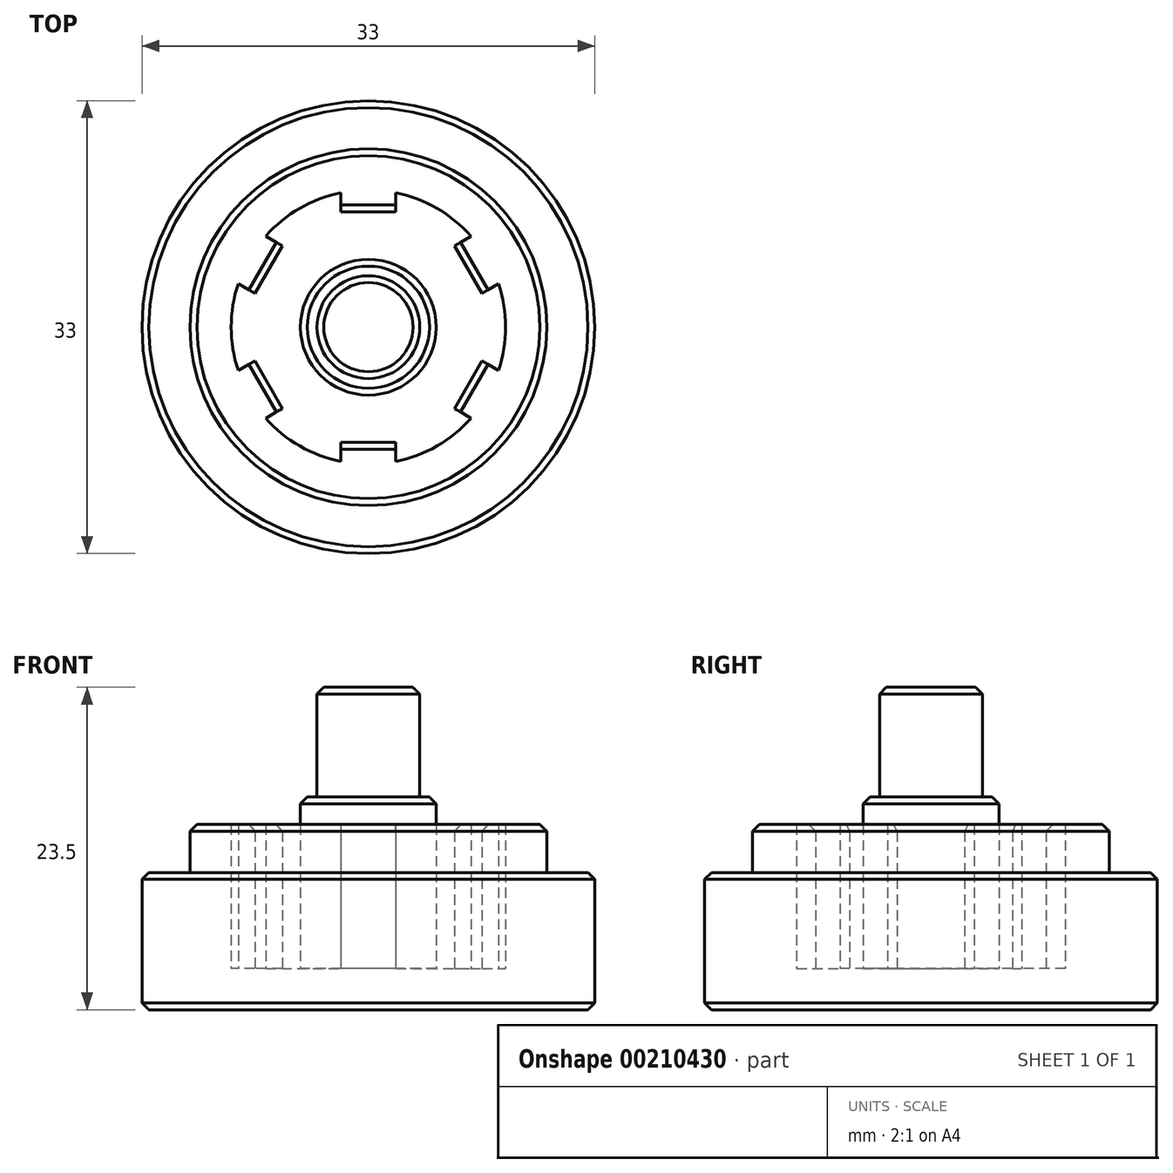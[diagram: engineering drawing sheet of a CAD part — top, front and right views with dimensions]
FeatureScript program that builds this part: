
annotation { "Feature Type Name" : "Feature", "Feature Type Description" : "" }
export const myFeature = defineFeature(function(context is Context, id is Id, definition is map)
    precondition{}
    {
        {
            var Q0;
            Q0=qCreatedBy(makeId("Top.planeOp"),FACE);
            var sketch = newSketch(context, id + "F0", { "sketchPlane" : qUnion([Q0])});
            skCircle(sketch, "E0", {"center": v(0, 0) * mm, "radius": 16.5 * mm});
            skSolve(sketch);
        }
        {
            var Q0;
            Q0 = qSketchRegion(id + "F0", true);
            extrude(context, id + "F1", {"entities" : qUnion([Q0]), "depth" : 10 * mm});
        }
        {
            var Q0;
            Q0=makeQuery(id+"F1.opExtrude","CAP_FACE",FACE,{"disambiguationData":[OSD([sQuery(id+"F0.wireOp",EDGE,"E0")])],"isStart":false});
            var sketch = newSketch(context, id + "F2", { "sketchPlane" : qUnion([Q0])});
            skArc(sketch, "E1", {"start": v(-2, 9.8) * mm, "mid": v(-5, 8.66) * mm, "end": v(-7.49, 6.63) * mm});
            skCircle(sketch, "E2", {"center": v(0, 0) * mm, "radius": 13 * mm});
            skLineSegment(sketch, "E3", {"start": v(-2, 9.8) * mm, "end": v(-2, 8.4) * mm});
            skLineSegment(sketch, "E4", {"start": v(-2, 8.4) * mm, "end": v(2, 8.4) * mm});
            skLineSegment(sketch, "E5", {"start": v(2, 8.4) * mm, "end": v(2, 9.8) * mm});
            skLineSegment(sketch, "E6.1.0", {"start": v(-8.27, 2.47) * mm, "end": v(-6.27, 5.93) * mm});
            skLineSegment(sketch, "E6.1.1", {"start": v(-6.27, 5.93) * mm, "end": v(-7.49, 6.63) * mm});
            skLineSegment(sketch, "E6.1.2", {"start": v(-9.49, 3.17) * mm, "end": v(-8.27, 2.47) * mm});
            skLineSegment(sketch, "E6.2.0", {"start": v(-6.27, -5.93) * mm, "end": v(-8.27, -2.47) * mm});
            skLineSegment(sketch, "E6.2.1", {"start": v(-8.27, -2.47) * mm, "end": v(-9.49, -3.17) * mm});
            skLineSegment(sketch, "E6.2.2", {"start": v(-7.49, -6.63) * mm, "end": v(-6.27, -5.93) * mm});
            skLineSegment(sketch, "E6.3.0", {"start": v(2, -8.4) * mm, "end": v(-2, -8.4) * mm});
            skLineSegment(sketch, "E6.3.1", {"start": v(-2, -8.4) * mm, "end": v(-2, -9.8) * mm});
            skLineSegment(sketch, "E6.3.2", {"start": v(2, -9.8) * mm, "end": v(2, -8.4) * mm});
            skLineSegment(sketch, "E6.4.0", {"start": v(8.27, -2.47) * mm, "end": v(6.27, -5.93) * mm});
            skLineSegment(sketch, "E6.4.1", {"start": v(6.27, -5.93) * mm, "end": v(7.49, -6.63) * mm});
            skLineSegment(sketch, "E6.4.2", {"start": v(9.49, -3.17) * mm, "end": v(8.27, -2.47) * mm});
            skLineSegment(sketch, "E6.5.0", {"start": v(6.27, 5.93) * mm, "end": v(8.27, 2.47) * mm});
            skLineSegment(sketch, "E6.5.1", {"start": v(8.27, 2.47) * mm, "end": v(9.49, 3.17) * mm});
            skLineSegment(sketch, "E6.5.2", {"start": v(7.49, 6.63) * mm, "end": v(6.27, 5.93) * mm});
            skArc(sketch, "E7.trimOffspring", {"start": v(7.49, 6.63) * mm, "mid": v(5, 8.66) * mm, "end": v(2, 9.8) * mm});
            skArc(sketch, "E8.trimOffspring", {"start": v(9.49, -3.17) * mm, "mid": v(10, 0) * mm, "end": v(9.49, 3.17) * mm});
            skArc(sketch, "E9.trimOffspring", {"start": v(2, -9.8) * mm, "mid": v(5, -8.66) * mm, "end": v(7.49, -6.63) * mm});
            skArc(sketch, "E10.trimOffspring", {"start": v(-7.49, -6.63) * mm, "mid": v(-5, -8.66) * mm, "end": v(-2, -9.8) * mm});
            skArc(sketch, "E11.trimOffspring", {"start": v(-9.49, 3.17) * mm, "mid": v(-10, 0) * mm, "end": v(-9.49, -3.17) * mm});
            skSolve(sketch);
        }
        {
            var Q0;
            Q0 = qSketchRegion(id + "F2", true);
            extrude(context, id + "F3", {"entities" : qUnion([Q0]), "operationType" : NewBodyOperationType.ADD, "depth" : 10.5 * mm});
        }
        {
            var Q0;
            Q0=makeQuery(id+"F3.opExtrude","CAP_EDGE",EDGE,{"disambiguationData":[OSD([sQuery(id+"F2.wireOp",EDGE,"E4")])],"isStart":false});
            var Q1;
            Q1=makeQuery(id+"F3.opExtrude","CAP_EDGE",EDGE,{"disambiguationData":[OSD([sQuery(id+"F2.wireOp",EDGE,"E6.1.0")])],"isStart":false});
            var Q2;
            Q2=makeQuery(id+"F3.opExtrude","CAP_EDGE",EDGE,{"disambiguationData":[OSD([sQuery(id+"F2.wireOp",EDGE,"E6.2.0")])],"isStart":false});
            var Q3;
            Q3=makeQuery(id+"F3.opExtrude","CAP_EDGE",EDGE,{"disambiguationData":[OSD([sQuery(id+"F2.wireOp",EDGE,"E6.3.0")])],"isStart":false});
            var Q4;
            Q4=makeQuery(id+"F3.opExtrude","CAP_EDGE",EDGE,{"disambiguationData":[OSD([sQuery(id+"F2.wireOp",EDGE,"E6.4.0")])],"isStart":false});
            var Q5;
            Q5=makeQuery(id+"F3.opExtrude","CAP_EDGE",EDGE,{"disambiguationData":[OSD([sQuery(id+"F2.wireOp",EDGE,"E6.5.0")])],"isStart":false});
            chamfer(context, id + "F4", {"entities" : qUnion([Q0, Q1, Q2, Q3, Q4, Q5]), "width" : .5 * mm, "tangentPropagation" : true});
        }
        {
            var Q0;
            Q0=makeQuery(id+"F3.boolean.opBoolean","SPLIT",FACE,{"disambiguationData":[TD([makeQuery(id+"F3.opExtrude","SWEPT_FACE",FACE,{"disambiguationData":[OSD([sQuery(id+"F2.wireOp",EDGE,"E1")])]})])],"derivedFrom":makeQuery(id+"F1.opExtrude","CAP_FACE",FACE,{"disambiguationData":[OSD([sQuery(id+"F0.wireOp",EDGE,"E0")])],"isStart":false})});
            var sketch = newSketch(context, id + "F5", { "sketchPlane" : qUnion([Q0])});
            skCircle(sketch, "E12", {"center": v(0, 0) * mm, "radius": 4.95 * mm});
            skSolve(sketch);
        }
        {
            var Q0;
            Q0 = qSketchRegion(id + "F5", true);
            extrude(context, id + "F6", {"entities" : qUnion([Q0]), "operationType" : NewBodyOperationType.ADD, "depth" : 12.5 * mm});
        }
        {
            var Q0;
            Q0=makeQuery(id+"F6.opExtrude","CAP_EDGE",EDGE,{"disambiguationData":[OSD([sQuery(id+"F5.wireOp",EDGE,"E12")])],"isStart":false});
            chamfer(context, id + "F7", {"entities" : qUnion([Q0]), "width" : .5 * mm, "tangentPropagation" : true});
        }
        {
            var Q0;
            Q0=makeQuery(id+"F6.opExtrude","CAP_FACE",FACE,{"disambiguationData":[OSD([sQuery(id+"F5.wireOp",EDGE,"E12")])],"isStart":false});
            var sketch = newSketch(context, id + "F8", { "sketchPlane" : qUnion([Q0])});
            skCircle(sketch, "E13", {"center": v(0, 0) * mm, "radius": 3.75 * mm});
            skSolve(sketch);
        }
        {
            var Q0;
            Q0 = qSketchRegion(id + "F8", true);
            extrude(context, id + "F9", {"entities" : qUnion([Q0]), "operationType" : NewBodyOperationType.ADD, "depth" : 8 * mm});
        }
        {
            var Q0;
            Q0=makeQuery(id+"F9.opExtrude","CAP_EDGE",EDGE,{"disambiguationData":[OSD([sQuery(id+"F8.wireOp",EDGE,"E13")])],"isStart":false});
            chamfer(context, id + "F10", {"entities" : qUnion([Q0]), "width" : .5 * mm, "tangentPropagation" : true});
        }
        {
            var Q0;
            {var subQ0=sQuery(id+"F0.wireOp",EDGE,"E0");Q0=makeQuery(id+"F3.boolean.opBoolean","SPLIT",FACE,{"disambiguationData":[TD([makeQuery(id+"F1.opExtrude","SWEPT_FACE",FACE,{"disambiguationData":[OSD([subQ0])]})])],"derivedFrom":makeQuery(id+"F1.opExtrude","CAP_FACE",FACE,{"disambiguationData":[OSD([subQ0])],"isStart":false})});}
            var sketch = newSketch(context, id + "F11", { "sketchPlane" : qUnion([Q0])});
            skCircle(sketch, "E14", {"center": v(0, 0) * mm, "radius": 16.5 * mm});
            skCircle(sketch, "E15", {"center": v(0, 0) * mm, "radius": 13 * mm});
            skSolve(sketch);
        }
        {
            var Q0;
            Q0 = qSketchRegion(id + "F11", true);
            extrude(context, id + "F12", {"entities" : qUnion([Q0]), "operationType" : NewBodyOperationType.ADD, "depth" : 7 * mm});
        }
        {
            var Q0;
            Q0=makeQuery(id+"F1.opExtrude","CAP_FACE",FACE,{"disambiguationData":[OSD([sQuery(id+"F0.wireOp",EDGE,"E0")])],"isStart":true});
            var sketch = newSketch(context, id + "F13", { "sketchPlane" : qUnion([Q0])});
            skCircle(sketch, "E16", {"center": v(0, 0) * mm, "radius": 25 * mm});
            skSolve(sketch);
        }
        {
            var Q0;
            Q0 = qSketchRegion(id + "F13", true);
            extrude(context, id + "F14", {"entities" : qUnion([Q0]), "operationType" : NewBodyOperationType.REMOVE, "oppositeDirection" : true, "depth" : 7 * mm});
        }
        {
            var Q0;
            Q0=makeQuery(id+"F3.opExtrude","CAP_EDGE",EDGE,{"disambiguationData":[OSD([sQuery(id+"F2.wireOp",EDGE,"E2")])],"isStart":false});
            var Q1;
            Q1=makeQuery(id+"F12.opExtrude","CAP_EDGE",EDGE,{"disambiguationData":[OSD([sQuery(id+"F11.wireOp",EDGE,"E14")])],"isStart":false});
            var Q2;
            Q2=makeQuery(id+"F14.boolean.opBoolean","COPY",EDGE,{"derivedFrom":makeQuery(id+"F14.opExtrude","CAP_EDGE",EDGE,{"disambiguationData":[OSD([sQuery(id+"F13.wireOp",EDGE,"E16")])],"isStart":false})});
            var Q3;
            Q3=makeQuery(id+"F14.boolean.opBoolean","INTERSECT",EDGE,{"derivedFrom":[makeQuery(id+"F12.boolean.opBoolean","MERGE",FACE,{"derivedFrom":[makeQuery(id+"F1.opExtrude","SWEPT_FACE",FACE,{"disambiguationData":[OSD([sQuery(id+"F0.wireOp",EDGE,"E0")])]}),makeQuery(id+"F12.opExtrude","SWEPT_FACE",FACE,{"disambiguationData":[OSD([sQuery(id+"F11.wireOp",EDGE,"E14")])]})]}),makeQuery(id+"F14.opExtrude","CAP_FACE",FACE,{"disambiguationData":[OSD([sQuery(id+"F13.wireOp",EDGE,"E16")])],"isStart":false})]});
            chamfer(context, id + "F15", {"entities" : qUnion([Q0, Q1, Q2, Q3]), "width" : .5 * mm, "tangentPropagation" : true});
        }
    });
